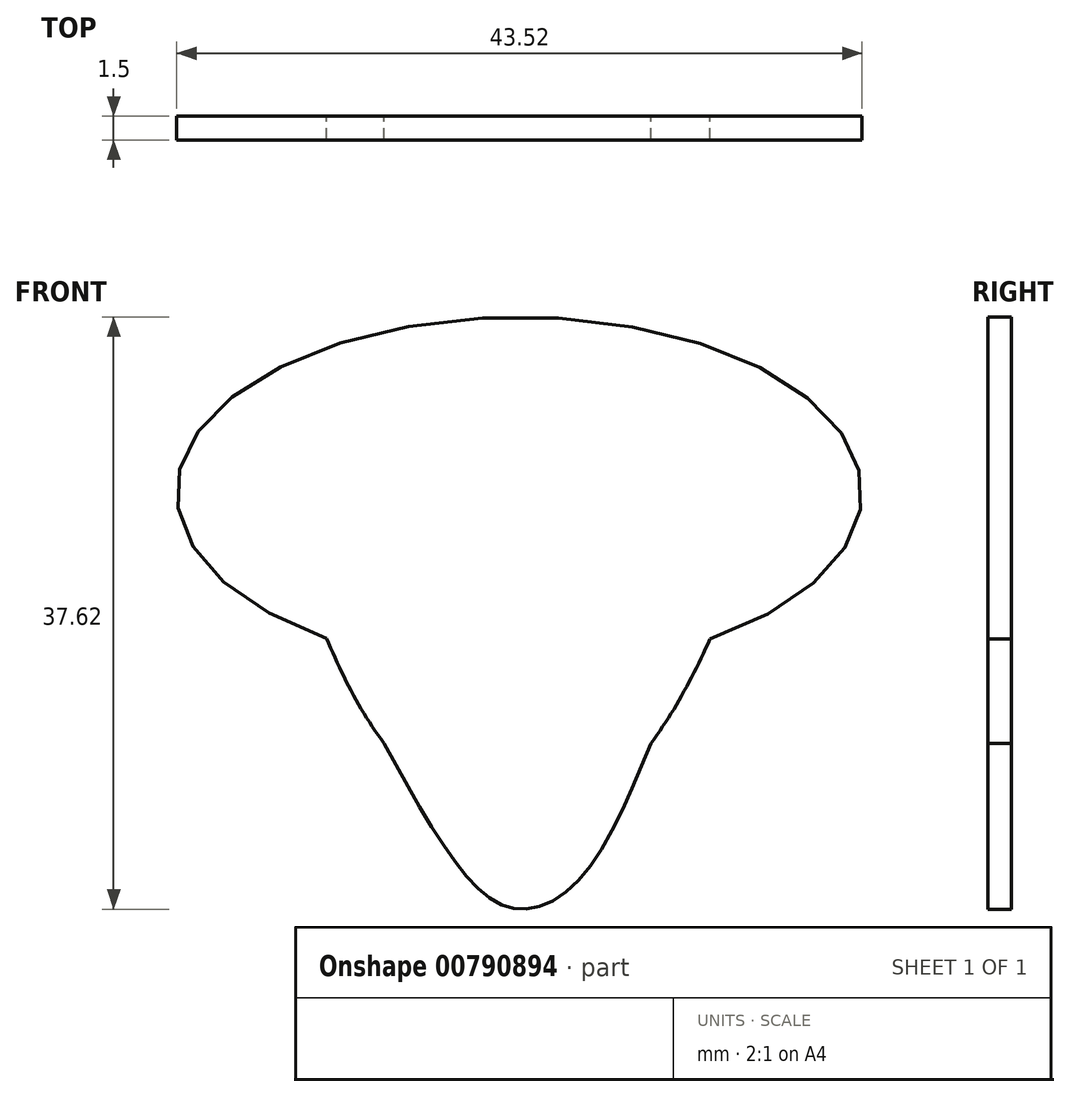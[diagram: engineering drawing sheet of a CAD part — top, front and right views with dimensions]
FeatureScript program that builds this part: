
annotation { "Feature Type Name" : "Feature", "Feature Type Description" : "" }
export const myFeature = defineFeature(function(context is Context, id is Id, definition is map)
    precondition{}
    {
        {
            var Q0;
            Q0=qCreatedBy(makeId("Front.planeOp"),FACE);
            var sketch = newSketch(context, id + "F0", { "sketchPlane" : qUnion([Q0])});
            skFitSpline(sketch, "E0", {"points": [v(-14.2, -3.95) * mm, v(-8.58, -15.91) * mm, v(0, -21.4) * mm, v(8.36, -15.91) * mm, v(14.63, -3.03) * mm], "startDerivative": vector(16.95, -48.27) * mm, "endDerivative": vector(19.2, 50.27) * mm});
            skFitSpline(sketch, "E1", {"points": [v(-8.58, -15.91) * mm, v(-3.32, -24.38) * mm, v(0, -26.44) * mm, v(3.78, -24.6) * mm, v(8.36, -15.91) * mm], "startDerivative": vector(17.37, -31.8) * mm, "endDerivative": vector(13.66, 33.4) * mm});
            skEllipticalArc(sketch, "E2", {});
            const initialGuessF0  = {"E2": [0, 0, -1, 0, 0.02175968512891273, 0.011167043509064502, 2.1610563911911114, 0.9734933504220084]};
            skSetInitialGuess(sketch, initialGuessF0);
            skSolve(sketch);
        }
        {
            var Q0;
            Q0 = qSketchRegion(id + "F0", true);
            extrude(context, id + "F1", {"entities" : qUnion([Q0]), "depth" : 1.5 * mm, "offsetDistance" : 25 * mm});
        }
    });
